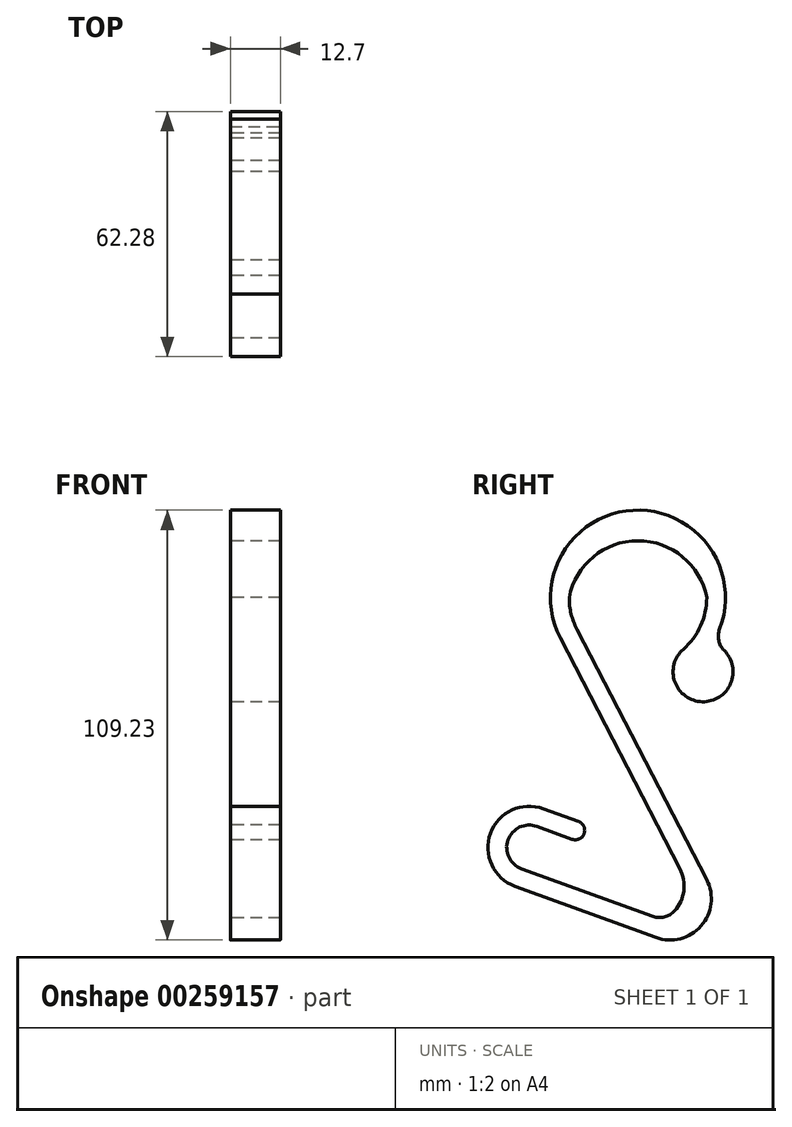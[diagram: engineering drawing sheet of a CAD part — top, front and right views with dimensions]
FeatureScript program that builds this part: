
annotation { "Feature Type Name" : "Feature", "Feature Type Description" : "" }
export const myFeature = defineFeature(function(context is Context, id is Id, definition is map)
    precondition{}
    {
        {
            var Q0;
            Q0=qCreatedBy(makeId("Right.planeOp"),FACE);
            var sketch = newSketch(context, id + "F0", { "sketchPlane" : qUnion([Q0])});
            skArc(sketch, "E0", {"start": v(-11.34, 9.85) * mm, "mid": v(-24.77, 3.58) * mm, "end": v(-18.5, -9.85) * mm});
            skLineSegment(sketch, "E1", {"start": v(-14.92, 0) * mm, "end": v(20.88, -13.03) * mm, "construction": true});
            skArc(sketch, "E2", {"start": v(17.3, -22.88) * mm, "mid": v(28.75, -19.95) * mm, "end": v(30.18, -8.21) * mm});
            skArc(sketch, "E3", {"start": v(24.23, 50.38) * mm, "mid": v(15.93, 80.66) * mm, "end": v(-2.8, 55.47) * mm});
            skLineSegment(sketch, "E4", {"start": v(-11.34, 9.85) * mm, "end": v(-2.39, 6.59) * mm});
            skPoint(sketch, "E5", {"position": v(-2.39, 6.59) * mm});
            skLineSegment(sketch, "E6", {"start": v(-18.5, -9.85) * mm, "end": v(17.3, -22.88) * mm});
            skLineSegment(sketch, "E7", {"start": v(-2.8, 55.47) * mm, "end": v(30.18, -8.21) * mm});
            skArc(sketch, "E8", {"start": v(24.23, 50.38) * mm, "mid": v(30.77, 37.19) * mm, "end": v(31.65, 51.9) * mm});
            skLineSegment(sketch, "E9", {"start": v(24.23, 50.38) * mm, "end": v(34.28, 38.93) * mm, "construction": true});
            skArc(sketch, "E10.1", {"start": v(31.65, 51.9) * mm, "mid": v(13.5, 85.71) * mm, "end": v(-7.03, 53.28) * mm});
            skLineSegment(sketch, "E10.2", {"start": v(-7.03, 53.28) * mm, "end": v(25.95, -10.4) * mm});
            skLineSegment(sketch, "E10.3", {"start": v(-12.97, 5.37) * mm, "end": v(-4.02, 2.11) * mm});
            skArc(sketch, "E10.4", {"start": v(-12.97, 5.37) * mm, "mid": v(-20.3, 1.95) * mm, "end": v(-16.88, -5.37) * mm});
            skLineSegment(sketch, "E10.5", {"start": v(-16.88, -5.37) * mm, "end": v(18.93, -18.4) * mm});
            skArc(sketch, "E10.6", {"start": v(18.93, -18.4) * mm, "mid": v(25.17, -16.8) * mm, "end": v(25.95, -10.4) * mm});
            skArc(sketch, "E11", {"start": v(-4.02, 2.11) * mm, "mid": v(-0.97, 3.54) * mm, "end": v(-2.39, 6.59) * mm});
            skSolve(sketch);
        }
        {
            var Q0;
            Q0=makeQuery(id+"F0.imprint","IMPRINT",FACE,{"disambiguationData":[TD([[makeQuery(id+"F0.imprint","IMPRINT",EDGE,{"derivedFrom":sQuery(id+"F0.wireOp",EDGE,"E0")}),1.0]])]});
            extrude(context, id + "F1", {"entities" : qUnion([Q0]), "endBound" : BoundingType.SYMMETRIC, "depth" : 12.7 * mm});
        }
        {
            var Q0;
            Q0=qCreatedBy(makeId("Right.planeOp"),FACE);
            var sketch = newSketch(context, id + "F2", { "sketchPlane" : qUnion([Q0])});
            skArc(sketch, "E12.0.0", {"start": v(31.65, 51.9) * mm, "mid": v(13.5, 85.71) * mm, "end": v(-7.03, 53.28) * mm, "construction": true});
            skLineSegment(sketch, "E12.0.1", {"start": v(23.36, -5.39) * mm, "end": v(25.95, -10.4) * mm});
            skArc(sketch, "E12.0.2", {"start": v(25.95, -10.4) * mm, "mid": v(25.17, -16.8) * mm, "end": v(18.93, -18.4) * mm});
            skLineSegment(sketch, "E12.0.3", {"start": v(18.93, -18.4) * mm, "end": v(-16.88, -5.37) * mm, "construction": true});
            skArc(sketch, "E12.0.4", {"start": v(-16.88, -5.37) * mm, "mid": v(-20.3, 1.95) * mm, "end": v(-12.97, 5.37) * mm, "construction": true});
            skLineSegment(sketch, "E12.0.5", {"start": v(-12.97, 5.37) * mm, "end": v(-4.02, 2.11) * mm, "construction": true});
            skArc(sketch, "E12.0.6", {"start": v(-4.02, 2.11) * mm, "mid": v(-0.97, 3.54) * mm, "end": v(-2.39, 6.59) * mm, "construction": true});
            skLineSegment(sketch, "E12.0.7", {"start": v(-2.39, 6.59) * mm, "end": v(-11.34, 9.85) * mm, "construction": true});
            skArc(sketch, "E12.0.8", {"start": v(-11.34, 9.85) * mm, "mid": v(-24.77, 3.58) * mm, "end": v(-18.5, -9.85) * mm, "construction": true});
            skLineSegment(sketch, "E12.0.9", {"start": v(-18.5, -9.85) * mm, "end": v(17.3, -22.88) * mm, "construction": true});
            skArc(sketch, "E12.0.10", {"start": v(17.3, -22.88) * mm, "mid": v(28.75, -19.95) * mm, "end": v(30.18, -8.21) * mm, "construction": true});
            skLineSegment(sketch, "E12.0.11", {"start": v(30.18, -8.21) * mm, "end": v(-2.8, 55.47) * mm, "construction": true});
            skArc(sketch, "E12.0.12", {"start": v(-4.76, 63.5) * mm, "mid": v(12.7, 80.96) * mm, "end": v(30.16, 63.5) * mm});
            skArc(sketch, "E12.0.13", {"start": v(24.23, 50.38) * mm, "mid": v(30.77, 37.19) * mm, "end": v(31.65, 51.9) * mm, "construction": true});
            skArc(sketch, "E13", {"start": v(18.93, -18.4) * mm, "mid": v(23.92, -12.84) * mm, "end": v(23.36, -5.39) * mm});
            skArc(sketch, "E14", {"start": v(30.16, 63.5) * mm, "mid": v(12.7, 77.93) * mm, "end": v(-4.76, 63.5) * mm});
            skSolve(sketch);
        }
        {
            var Q0;
            Q0 = qSketchRegion(id + "F2", true);
            extrude(context, id + "F3", {"entities" : qUnion([Q0]), "operationType" : NewBodyOperationType.ADD, "endBound" : BoundingType.SYMMETRIC, "depth" : 12.7 * mm});
        }
        {
            var Q0;
            Q0=makeQuery(id+"F1.opExtrude","SWEPT_EDGE",EDGE,{"disambiguationData":[OSD([sQuery(id+"F0.wireOp",EDGE,"E8"),sQuery(id+"F0.wireOp",EDGE,"E10.1")])]});
            fillet(context, id + "F4", {"entities" : qUnion([Q0]), "radius" : 5.08 * mm, "tangentPropagation" : true, "allowEdgeOverflow" : false});
        }
        {
            var Q0;
            Q0=makeQuery(id+"F3.boolean.opBoolean","MERGE",EDGE,{"derivedFrom":[makeQuery(id+"F1.opExtrude","SWEPT_EDGE",EDGE,{"disambiguationData":[OSD([sQuery(id+"F0.wireOp",EDGE,"E10.5"),sQuery(id+"F0.wireOp",EDGE,"E10.6")])]}),makeQuery(id+"F3.opExtrude","SWEPT_EDGE",EDGE,{"disambiguationData":[OSD([sQuery(id+"F2.wireOp",EDGE,"E12.0.2"),sQuery(id+"F2.wireOp",EDGE,"E13")])]})]});
            fillet(context, id + "F5", {"entities" : qUnion([Q0]), "radius" : 5.08 * mm, "tangentPropagation" : true, "allowEdgeOverflow" : false});
        }
    });
